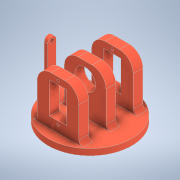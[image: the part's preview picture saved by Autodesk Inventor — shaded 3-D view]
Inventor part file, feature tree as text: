
AUTODESK INVENTOR PART (.ipt)
format: ipt  version: 2021 (Build 250183000, 183)  size: 325,632 bytes
history: native  units: mm
features: extrude x11, sketch x9, projected_geometry x5, fillet x3
ambient origin geometry x8: Origin, YZ Plane, XZ Plane, XY Plane, X Axis, Y Axis, Z Axis, Center Point
bodies: Body1 (feature_tree)
feature tree (28):
  extrude  "Extrusion2"  Depth=4.5mm TaperAngle=0.0deg
  extrude  "Extrusion3"  Depth=30.0mm
  fillet  "Fillet1"  Radius=12.5mm
  fillet  "Fillet2"  Radius=7.0mm
  extrude  "Extrusion4"  Depth=30.0mm
  extrude  "Extrusion5"  Depth=3.0mm
  extrude  "Extrusion6"  Depth=10.0mm
  extrude  "Extrusion7"  Depth=10.0mm TaperAngle=0.0deg
  sketch  "Sketch8"  dims[d20=15.0mm d21=5.0mm]
  extrude  "Extrusion8"  Depth=5.0mm
  extrude  "Extrusion9"  Depth=15.0mm
  extrude  "Extrusion10"  Depth=10.0mm
  extrude  "Extrusion11"  Depth=10.0mm
  fillet  "Fillet3"  Radius=46.0mm
  extrude  "Extrusion12"  Depth=10.0mm TaperAngle=0.0deg
  sketch  "Sketch2"  dims[d3=60.0mm d4=4.5mm d5=0.0mm]
  sketch  "Sketch3"  dims[d6=30.0mm d7=7.0mm d8=12.5mm d9=7.0mm]
  sketch  "Sketch4"  dims[d10=30.0mm d11=7.0mm]
  sketch  "Sketch5"  dims[d12=35.0mm d13=0.0mm d14=3.0mm]
  projected_geometry  "Projected Loop1"
  sketch  "Sketch6"  dims[d15=10.0mm d16=12.5mm]
  sketch  "Sketch7"  dims[d17=3.0mm d18=10.0mm d19=0.0mm]
  projected_geometry  "Projected Loop2"
  projected_geometry  "Projected Loop3"
  sketch  "Sketch9"  dims[d22=2.0mm d23=15.0mm]
  projected_geometry  "Projected Loop4"
  sketch  "Sketch10"  dims[d24=5.0mm d25=2.5mm d26=2.0mm d27=46.0mm d28=0.0mm d29=7.0mm d30=0.0mm d31=12.5mm d32=22.5mm d33=7.0mm d34=0.0mm d35=11.25mm d36=15.0mm d37=7.0mm d38=0.0mm d39=10.0mm d40=0.0mm d41=7.0mm d42=0.0mm d45=2.5mm d46=6.0mm d47=35.0mm d48=0.0mm d49=3.0mm d51=6.0mm d52=3.0mm d53=10.0mm d54=0.0mm]
  projected_geometry  "Projected Loop5"
